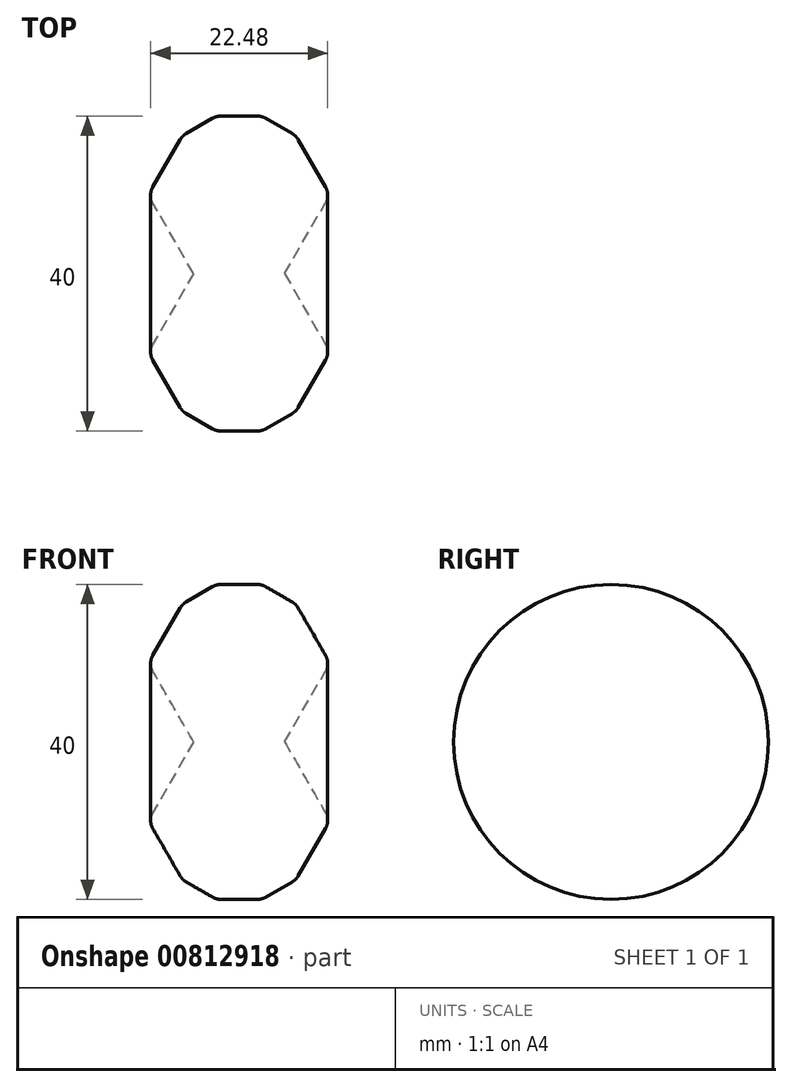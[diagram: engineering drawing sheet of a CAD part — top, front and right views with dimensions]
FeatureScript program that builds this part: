
annotation { "Feature Type Name" : "Feature", "Feature Type Description" : "" }
export const myFeature = defineFeature(function(context is Context, id is Id, definition is map)
    precondition{}
    {
        {
            var Q0;
            Q0=qCreatedBy(makeId("Front.planeOp"),FACE);
            var sketch = newSketch(context, id + "F0", { "sketchPlane" : qUnion([Q0])});
            skCircle(sketch, "E0.cCircle", {"center": v(0, -10) * mm, "radius": 10 * mm, "construction": true});
            skLineSegment(sketch, "E0.0", {"start": v(-5.77, 0) * mm, "end": v(5.77, 0) * mm});
            skLineSegment(sketch, "E0.1", {"start": v(5.77, 0) * mm, "end": v(11.55, -10) * mm});
            skLineSegment(sketch, "E0.2", {"start": v(11.55, -10) * mm, "end": v(5.77, -20) * mm});
            skLineSegment(sketch, "E0.3", {"start": v(5.77, -20) * mm, "end": v(-5.77, -20) * mm});
            skLineSegment(sketch, "E0.4", {"start": v(-5.77, -20) * mm, "end": v(-11.55, -10) * mm});
            skLineSegment(sketch, "E0.5", {"start": v(-11.55, -10) * mm, "end": v(-5.77, 0) * mm});
            skPoint(sketch, "E0.0.midPoint", {"position": v(0, 0) * mm});
            skSolve(sketch);
        }
        {
            var Q0;
            Q0=makeQuery(id+"F0.imprint","IMPRINT",FACE,{"disambiguationData":[TD([[makeQuery(id+"F0.imprint","IMPRINT",EDGE,{"derivedFrom":sQuery(id+"F0.wireOp",EDGE,"E0.0")}),-1.0]])]});
            var Q1;
            Q1=sQuery(id+"F0.wireOp",EDGE,"E0.3");
            revolve(context, id + "F1", {"surfaceOperationType" : NewSurfaceOperationType.NEW, "entities" : qUnion([Q0]), "axis" : qUnion([Q1]), "revolveType" : RevolveType.FULL});
        }
        {
            var Q0;
            Q0=makeQuery(id+"F1.opRevolve","SWEPT_FACE",FACE,{"disambiguationData":[OSD([sQuery(id+"F0.wireOp",EDGE,"E0.0")])]});
            chamfer(context, id + "F2", {"entities" : qUnion([Q0]), "width" : 5 * mm, "tangentPropagation" : true});
        }
        {
            var Q0;
            Q0=makeQuery(id+"F1.opRevolve","SWEPT_EDGE",EDGE,{"disambiguationData":[OSD([sQuery(id+"F0.wireOp",EDGE,"E0.4"),sQuery(id+"F0.wireOp",EDGE,"E0.5")])]});
            var Q1;
            {var subQ0=sQuery(id+"F0.wireOp",EDGE,"E0.5");Q1=makeQuery(id+"F2.opChamfer","BLEND_EDGE",EDGE,{"blendedFrom":[makeQuery(id+"F1.opRevolve","SWEPT_EDGE",EDGE,{"disambiguationData":[OSD([sQuery(id+"F0.wireOp",EDGE,"E0.0"),subQ0])]}),makeQuery(id+"F1.opRevolve","SWEPT_FACE",FACE,{"disambiguationData":[OSD([subQ0])]})],"blendedInto":[makeQuery(id+"F1.opRevolve","SWEPT_FACE",FACE,{"disambiguationData":[OSD([subQ0])]})]});}
            var Q2;
            {var subQ0=sQuery(id+"F0.wireOp",EDGE,"E0.0");Q2=makeQuery(id+"F2.opChamfer","BLEND_EDGE",EDGE,{"blendedFrom":[makeQuery(id+"F1.opRevolve","SWEPT_EDGE",EDGE,{"disambiguationData":[OSD([subQ0,sQuery(id+"F0.wireOp",EDGE,"E0.5")])]}),makeQuery(id+"F1.opRevolve","SWEPT_FACE",FACE,{"disambiguationData":[OSD([subQ0])]})],"blendedInto":[makeQuery(id+"F1.opRevolve","SWEPT_FACE",FACE,{"disambiguationData":[OSD([subQ0])]})]});}
            var Q3;
            {var subQ0=sQuery(id+"F0.wireOp",EDGE,"E0.0");Q3=makeQuery(id+"F2.opChamfer","BLEND_EDGE",EDGE,{"blendedFrom":[makeQuery(id+"F1.opRevolve","SWEPT_EDGE",EDGE,{"disambiguationData":[OSD([subQ0,sQuery(id+"F0.wireOp",EDGE,"E0.1")])]}),makeQuery(id+"F1.opRevolve","SWEPT_FACE",FACE,{"disambiguationData":[OSD([subQ0])]})],"blendedInto":[makeQuery(id+"F1.opRevolve","SWEPT_FACE",FACE,{"disambiguationData":[OSD([subQ0])]})]});}
            var Q4;
            {var subQ0=sQuery(id+"F0.wireOp",EDGE,"E0.1");Q4=makeQuery(id+"F2.opChamfer","BLEND_EDGE",EDGE,{"blendedFrom":[makeQuery(id+"F1.opRevolve","SWEPT_EDGE",EDGE,{"disambiguationData":[OSD([sQuery(id+"F0.wireOp",EDGE,"E0.0"),subQ0])]}),makeQuery(id+"F1.opRevolve","SWEPT_FACE",FACE,{"disambiguationData":[OSD([subQ0])]})],"blendedInto":[makeQuery(id+"F1.opRevolve","SWEPT_FACE",FACE,{"disambiguationData":[OSD([subQ0])]})]});}
            var Q5;
            Q5=makeQuery(id+"F1.opRevolve","SWEPT_EDGE",EDGE,{"disambiguationData":[OSD([sQuery(id+"F0.wireOp",EDGE,"E0.1"),sQuery(id+"F0.wireOp",EDGE,"E0.2")])]});
            var Q6;
            Q6=makeQuery(id+"F1.opRevolve","SWEPT_FACE",FACE,{"disambiguationData":[OSD([sQuery(id+"F0.wireOp",EDGE,"E0.2")])]});
            fillet(context, id + "F3", {"entities" : qUnion([Q0, Q1, Q2, Q3, Q4, Q5, Q6]), "radius" : 2 * mm, "tangentPropagation" : true, "allowEdgeOverflow" : false});
        }
    });
